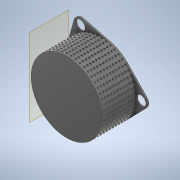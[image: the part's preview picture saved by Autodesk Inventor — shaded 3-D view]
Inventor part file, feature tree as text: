
AUTODESK INVENTOR PART (.ipt)
format: ipt  version: 2020 (Build 240168000, 168)  size: 1,446,912 bytes
history: native  units: in
note: dims shown in document units (in); Inventor stores cm internally (conversion verified against a paired STEP export)
features: sketch x4, extrude x2, projected_geometry x2, shell x1, plane x1, hole x1, pattern_circular x1
ambient origin geometry x8: Origin, YZ Plane, XZ Plane, XY Plane, X Axis, Y Axis, Z Axis, Center Point
bodies: Solid1 (feature_tree)
feature tree (12):
  extrude  "Extrusion1"  Depth=1.378in
  shell  "Shell1"  Thickness=1.378in
  plane  "Work Plane1"
  hole  "Hole1"  [1 undecoded]
  pattern_circular  "Circular Pattern1"  Count=11  [1 undecoded]
  sketch  "Sketch3"  dims[d6=0.0984in d7=4.3307in d9=0.1181in d10=0.3937in d12=0.3937in]
  extrude  "Extrusion2"  Depth=0.0591in TaperAngle=360.0deg
  sketch  "Sketch1"  dims[d0=2.5197in d1=0.1181in d2=1.378in d3=0.0in]
  sketch  "Sketch2"  dims[d4=0.0591in d5=0.0591in]
  projected_geometry  "Projected Loop1"
  sketch  "Sketch4"  dims[d14=0.0591in d15=0.2362in d16=0.1575in d17=0.0787in d18=90.0deg d19=0.315in d20=0.8108in d21=9.8425in d22=360.0deg d24=120.0deg d25=120.0deg d26=0.378in d27=1.5748in d28=1.5748in d29=1.5748in d30=0.378in d31=0.378in d32=0.0591in d33=0.0591in d34=0.0591in d35=0.0591in d36=0.0in]
  projected_geometry  "Projected Loop2"
note: 2 required parameter values undecoded (feature->parameter linkage not recoverable at this tier; creation-order binding heuristic only, values carry confidence <= 0.55)
